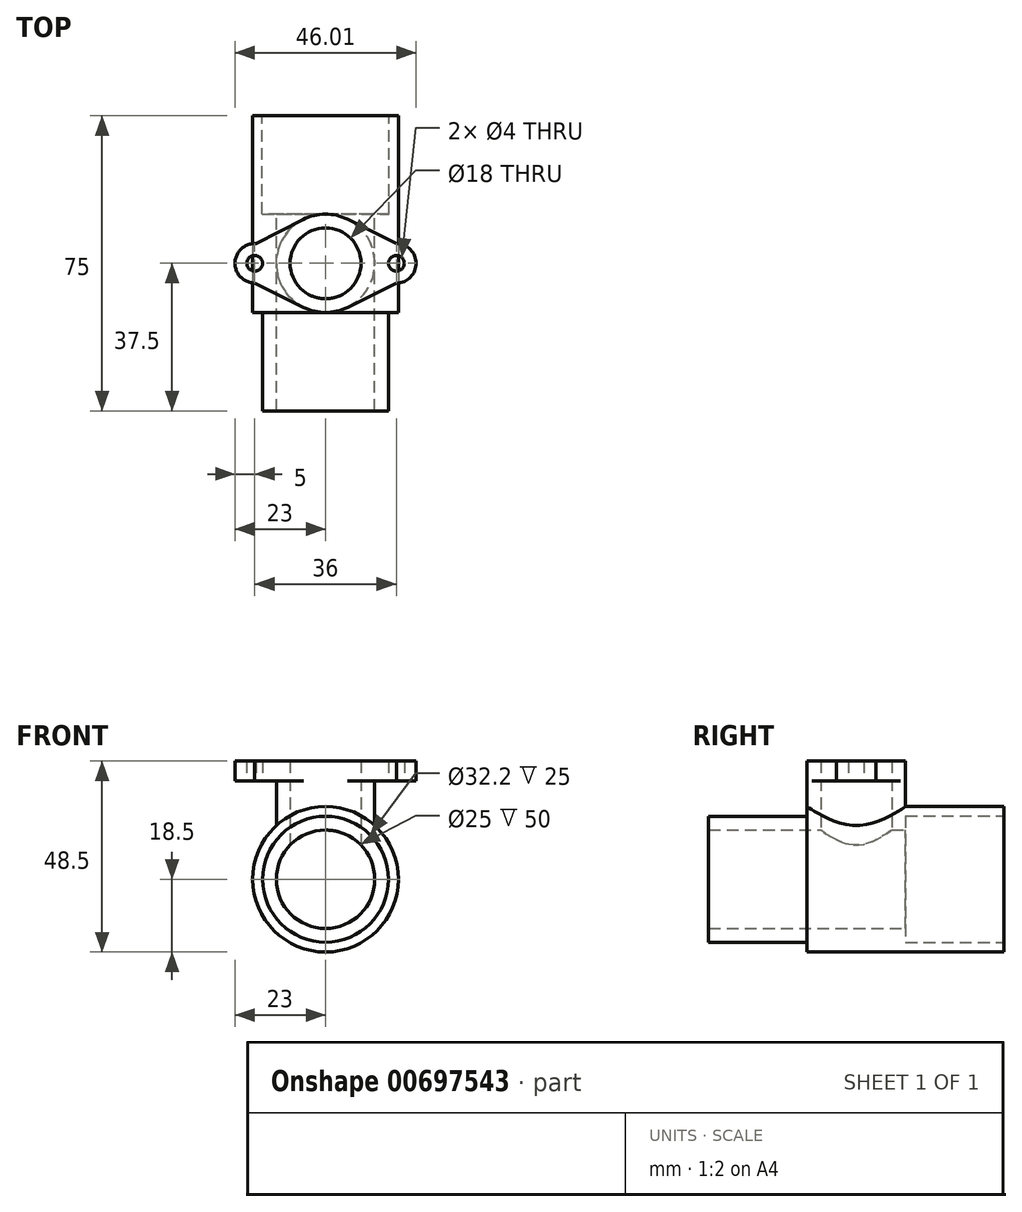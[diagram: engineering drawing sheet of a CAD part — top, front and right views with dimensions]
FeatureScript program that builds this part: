
annotation { "Feature Type Name" : "Feature", "Feature Type Description" : "" }
export const myFeature = defineFeature(function(context is Context, id is Id, definition is map)
    precondition{}
    {
        {
            var Q0;
            Q0=qCreatedBy(makeId("Front.planeOp"),FACE);
            var sketch = newSketch(context, id + "F0", { "sketchPlane" : qUnion([Q0])});
            skCircle(sketch, "E0", {"center": v(0, 0) * mm, "radius": 16 * mm});
            skCircle(sketch, "E1", {"center": v(0, 0) * mm, "radius": 18.5 * mm});
            skCircle(sketch, "E2", {"center": v(0, 0) * mm, "radius": 12.5 * mm});
            skSolve(sketch);
        }
        {
            var Q0;
            Q0=makeQuery(id+"F0.imprint","IMPRINT",FACE,{"disambiguationData":[TD([[makeQuery(id+"F0.imprint","IMPRINT",EDGE,{"derivedFrom":sQuery(id+"F0.wireOp",EDGE,"E0")}),1.0]])]});
            extrude(context, id + "F1", {"entities" : qUnion([Q0]), "depth" : 25 * mm, "offsetDistance" : 25 * mm});
        }
        {
            var Q0;
            Q0 = qSketchRegion(id + "F0", true);
            var Q1;
            Q1=makeQuery(id+"F1.opExtrude","CAP_FACE",FACE,{"disambiguationData":[OSD([sQuery(id+"F0.wireOp",EDGE,"E0")])],"isStart":true});
            extrude(context, id + "F2", {"entities" : qUnion([Q0, Q1]), "operationType" : NewBodyOperationType.ADD, "oppositeDirection" : true, "depth" : 50 * mm, "offsetDistance" : 25 * mm});
        }
        {
            var Q0;
            {var subQ0=sQuery(id+"F0.wireOp",EDGE,"E0");Q0=makeQuery(id+"F2.boolean.opBoolean","MERGE",FACE,{"derivedFrom":[makeQuery(id+"F2.opExtrude","CAP_FACE",FACE,{"disambiguationData":[OSD([subQ0,sQuery(id+"F0.wireOp",EDGE,"E1")])],"isStart":false}),makeQuery(id+"F2.opExtrude","CAP_FACE",FACE,{"disambiguationData":[OSD([subQ0])],"isStart":false})]});}
            var sketch = newSketch(context, id + "F3", { "sketchPlane" : qUnion([Q0])});
            skCircle(sketch, "E3", {"center": v(0, 0) * mm, "radius": 16.1 * mm});
            skSolve(sketch);
        }
        {
            var Q0;
            Q0=makeQuery(id+"F3.imprint","IMPRINT",FACE,{"disambiguationData":[TD([[makeQuery(id+"F3.imprint","IMPRINT",EDGE,{"derivedFrom":sQuery(id+"F3.wireOp",EDGE,"E3")}),1.0]])]});
            extrude(context, id + "F4", {"entities" : qUnion([Q0]), "operationType" : NewBodyOperationType.REMOVE, "oppositeDirection" : true, "depth" : 25 * mm, "offsetDistance" : 25 * mm});
        }
        {
            var Q0;
            Q0=qCreatedBy(makeId("Top.planeOp"),FACE);
            var sketch = newSketch(context, id + "F5", { "sketchPlane" : qUnion([Q0])});
            skCircle(sketch, "E4", {"center": v(0, 12.5) * mm, "radius": 12.5 * mm});
            skCircle(sketch, "E5", {"center": v(0, 12.5) * mm, "radius": 9 * mm});
            skSolve(sketch);
        }
        {
            var Q0;
            Q0 = qSketchRegion(id + "F5", true);
            extrude(context, id + "F6", {"entities" : qUnion([Q0]), "operationType" : NewBodyOperationType.ADD, "depth" : 25 * mm, "offsetDistance" : 25 * mm});
        }
        {
            var Q0;
            Q0=qCreatedBy(makeId("Front.planeOp"),FACE);
            var sketch = newSketch(context, id + "F7", { "sketchPlane" : qUnion([Q0])});
            skCircle(sketch, "E6", {"center": v(0, 0) * mm, "radius": 12.5 * mm});
            skSolve(sketch);
        }
        {
            var Q0;
            Q0 = qSketchRegion(id + "F7", true);
            extrude(context, id + "F8", {"entities" : qUnion([Q0]), "operationType" : NewBodyOperationType.REMOVE, "endBound" : BoundingType.SYMMETRIC, "depth" : 100 * mm, "offsetDistance" : 25 * mm});
        }
        {
            var Q0;
            Q0=makeQuery(id+"F6.opExtrude","CAP_FACE",FACE,{"disambiguationData":[OSD([sQuery(id+"F5.wireOp",EDGE,"E4"),sQuery(id+"F5.wireOp",EDGE,"E5")])],"isStart":false});
            var sketch = newSketch(context, id + "F9", { "sketchPlane" : qUnion([Q0])});
            skCircle(sketch, "E7", {"center": v(0, 12.5) * mm, "radius": 9 * mm});
            skSolve(sketch);
        }
        {
            var Q0;
            Q0 = qSketchRegion(id + "F9", true);
            extrude(context, id + "F10", {"entities" : qUnion([Q0]), "operationType" : NewBodyOperationType.REMOVE, "oppositeDirection" : true, "depth" : 30 * mm, "offsetDistance" : 25 * mm});
        }
        {
            var Q0;
            Q0=makeQuery(id+"F6.opExtrude","CAP_FACE",FACE,{"disambiguationData":[OSD([sQuery(id+"F5.wireOp",EDGE,"E4"),sQuery(id+"F5.wireOp",EDGE,"E5")])],"isStart":false});
            var sketch = newSketch(context, id + "F11", { "sketchPlane" : qUnion([Q0])});
            skCircle(sketch, "E8", {"center": v(-18, 12.5) * mm, "radius": 2 * mm});
            skCircle(sketch, "E9", {"center": v(18, 12.5) * mm, "radius": 2 * mm});
            skLineSegment(sketch, "E10", {"start": v(-18.08, 7.5) * mm, "end": v(-5.54, 1.3) * mm});
            skLineSegment(sketch, "E11", {"start": v(-17.7, 17.5) * mm, "end": v(-5.7, 23.63) * mm});
            skLineSegment(sketch, "E12", {"start": v(18.09, 17.5) * mm, "end": v(5.54, 23.7) * mm});
            skLineSegment(sketch, "E13", {"start": v(18.09, 7.5) * mm, "end": v(5.54, 1.3) * mm});
            skArc(sketch, "E14", {"start": v(-5.54, 1.3) * mm, "mid": v(0, 0) * mm, "end": v(5.54, 1.3) * mm});
            skArc(sketch, "E15", {"start": v(5.54, 23.7) * mm, "mid": v(-0.08, 25) * mm, "end": v(-5.7, 23.63) * mm});
            skArc(sketch, "E16", {"start": v(18.09, 7.5) * mm, "mid": v(23, 12.5) * mm, "end": v(18.09, 17.5) * mm});
            skArc(sketch, "E17", {"start": v(-17.7, 17.5) * mm, "mid": v(-23, 12.7) * mm, "end": v(-18.08, 7.5) * mm});
            skSolve(sketch);
        }
        {
            var Q0;
            Q0=makeQuery(id+"F11.imprint","IMPRINT",FACE,{"disambiguationData":[TD([[makeQuery(id+"F11.imprint","IMPRINT",EDGE,{"derivedFrom":sQuery(id+"F11.wireOp",EDGE,"E8")}),-1.0]])]});
            var Q1;
            {var subQ1=sQuery(id+"F11.wireOp",EDGE,"E14");Q1=makeQuery(id+"F11.imprint","IMPRINT",FACE,{"disambiguationData":[TD([[makeQuery(id+"F11.imprint","IMPRINT",EDGE,{"derivedFrom":subQ1}),1.0]])]});}
            var Q2;
            Q2=makeQuery(id+"F11.imprint","IMPRINT",FACE,{"disambiguationData":[TD([[makeQuery(id+"F11.imprint","IMPRINT",EDGE,{"derivedFrom":sQuery(id+"F11.wireOp",EDGE,"E9")}),-1.0]])]});
            extrude(context, id + "F12", {"entities" : qUnion([Q0, Q1, Q2]), "operationType" : NewBodyOperationType.ADD, "depth" : 5 * mm, "offsetDistance" : 25 * mm});
        }
    });
